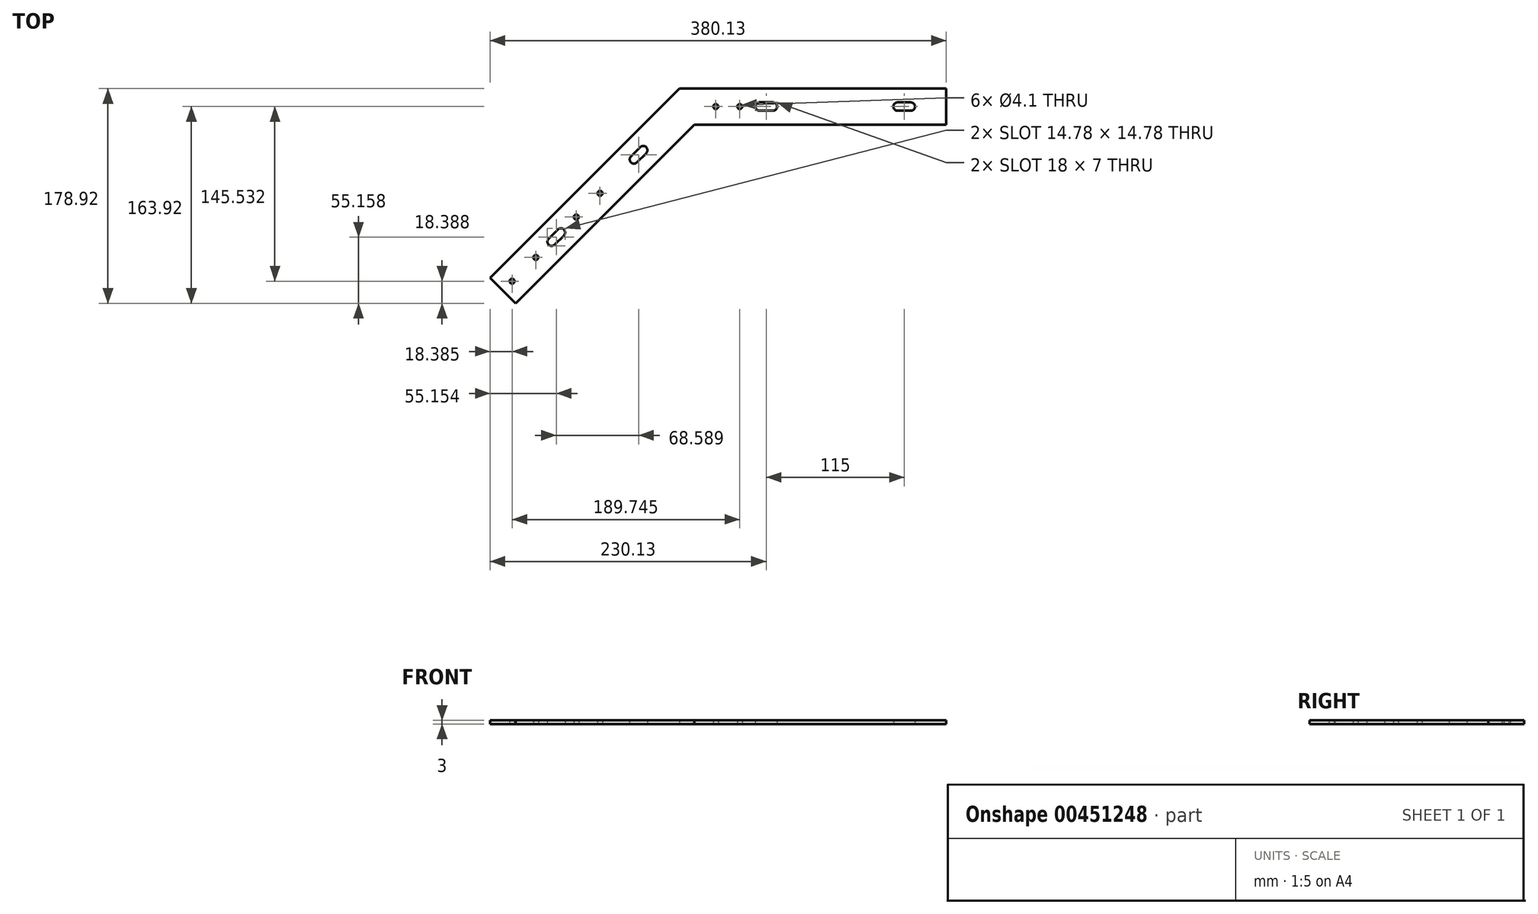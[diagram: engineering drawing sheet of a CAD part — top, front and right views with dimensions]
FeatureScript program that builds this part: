
annotation { "Feature Type Name" : "Feature", "Feature Type Description" : "" }
export const myFeature = defineFeature(function(context is Context, id is Id, definition is map)
    precondition{}
    {
        {
            var Q0;
            Q0=qCreatedBy(makeId("Top.planeOp"),FACE);
            var sketch = newSketch(context, id + "F0", { "sketchPlane" : qUnion([Q0])});
            skLineSegment(sketch, "E0", {"start": v(0, 0) * mm, "end": v(0, 30) * mm});
            skLineSegment(sketch, "E1", {"start": v(0, 30) * mm, "end": v(-222.43, 30) * mm});
            skLineSegment(sketch, "E2", {"start": v(-222.43, 30) * mm, "end": v(-380.13, -127.7) * mm});
            skLineSegment(sketch, "E3", {"start": v(-380.13, -127.7) * mm, "end": v(-358.92, -148.92) * mm});
            skLineSegment(sketch, "E4", {"start": v(-358.92, -148.92) * mm, "end": v(-210, 0) * mm});
            skLineSegment(sketch, "E5", {"start": v(0, 0) * mm, "end": v(-210, 0) * mm});
            skLineSegment(sketch, "E6", {"start": v(-222.43, 30) * mm, "end": v(-210, 0) * mm, "construction": true});
            skPoint(sketch, "E7.centerSnap0", {"position": v(0, 15) * mm});
            skCircle(sketch, "E8", {"center": v(-324.98, -93.76) * mm, "radius": 3.5 * mm, "construction": true});
            skLineSegment(sketch, "E9.bottom", {"start": v(-29.5, 11.5) * mm, "end": v(-40.5, 11.5) * mm});
            skLineSegment(sketch, "E9.top", {"start": v(-29.5, 18.5) * mm, "end": v(-40.5, 18.5) * mm});
            skLineSegment(sketch, "E9.left", {"start": v(-29.5, 11.5) * mm, "end": v(-29.5, 18.5) * mm});
            skLineSegment(sketch, "E9.right", {"start": v(-40.5, 11.5) * mm, "end": v(-40.5, 18.5) * mm});
            skPoint(sketch, "E9.middle", {"position": v(-35, 15) * mm});
            skArc(sketch, "E10", {"start": v(-40.5, 18.5) * mm, "mid": v(-44, 15) * mm, "end": v(-40.5, 11.5) * mm});
            skArc(sketch, "E11", {"start": v(-29.5, 11.5) * mm, "mid": v(-26, 15) * mm, "end": v(-29.5, 18.5) * mm});
            skLineSegment(sketch, "E12.bottom", {"start": v(-144.5, 11.5) * mm, "end": v(-155.5, 11.5) * mm});
            skLineSegment(sketch, "E12.top", {"start": v(-144.5, 18.5) * mm, "end": v(-155.5, 18.5) * mm});
            skLineSegment(sketch, "E12.left", {"start": v(-144.5, 11.5) * mm, "end": v(-144.5, 18.5) * mm});
            skLineSegment(sketch, "E12.right", {"start": v(-155.5, 11.5) * mm, "end": v(-155.5, 18.5) * mm});
            skPoint(sketch, "E12.middle", {"position": v(-150, 15) * mm});
            skArc(sketch, "E13", {"start": v(-155.5, 18.5) * mm, "mid": v(-159, 15) * mm, "end": v(-155.5, 11.5) * mm});
            skArc(sketch, "E14", {"start": v(-144.5, 11.5) * mm, "mid": v(-141, 15) * mm, "end": v(-144.5, 18.5) * mm});
            skLineSegment(sketch, "E15.bottom", {"start": v(-318.61, -92.35) * mm, "end": v(-326.39, -100.13) * mm});
            skLineSegment(sketch, "E15.top", {"start": v(-323.56, -87.4) * mm, "end": v(-331.34, -95.18) * mm});
            skLineSegment(sketch, "E15.left", {"start": v(-318.61, -92.35) * mm, "end": v(-323.56, -87.4) * mm});
            skLineSegment(sketch, "E15.right", {"start": v(-326.39, -100.13) * mm, "end": v(-331.34, -95.18) * mm});
            skArc(sketch, "E16", {"start": v(-331.34, -95.18) * mm, "mid": v(-331.34, -100.13) * mm, "end": v(-326.39, -100.13) * mm});
            skArc(sketch, "E17", {"start": v(-318.61, -92.35) * mm, "mid": v(-318.61, -87.4) * mm, "end": v(-323.56, -87.4) * mm});
            skCircle(sketch, "E18", {"center": v(-172, 15) * mm, "radius": 2.05 * mm});
            skCircle(sketch, "E19", {"center": v(-341.95, -110.73) * mm, "radius": 2.05 * mm});
            skCircle(sketch, "E20", {"center": v(-192, 15) * mm, "radius": 2.05 * mm});
            skLineSegment(sketch, "E21", {"start": v(-210, 0) * mm, "end": v(-164.47, 45.53) * mm, "construction": true});
            skLineSegment(sketch, "E22", {"start": v(-222.43, 30) * mm, "end": v(-201.21, 51.21) * mm, "construction": true});
            skLineSegment(sketch, "E23", {"start": v(-180, 30) * mm, "end": v(-201.21, 51.21) * mm, "construction": true});
            skLineSegment(sketch, "E24", {"start": v(-210, 0) * mm, "end": v(-290.3, 0) * mm, "construction": true});
            skCircle(sketch, "E25", {"center": v(-361.75, -130.53) * mm, "radius": 2.05 * mm});
            skCircle(sketch, "E26", {"center": v(-288.49, -57.28) * mm, "radius": 2.05 * mm});
            skCircle(sketch, "E27", {"center": v(-308.29, -77.07) * mm, "radius": 2.05 * mm});
            skCircle(sketch, "E28", {"center": v(-256.39, -25.17) * mm, "radius": 3.5 * mm, "construction": true});
            skLineSegment(sketch, "E29.bottom", {"start": v(-250.02, -23.76) * mm, "end": v(-257.8, -31.54) * mm});
            skLineSegment(sketch, "E29.top", {"start": v(-254.97, -18.8) * mm, "end": v(-262.75, -26.59) * mm});
            skLineSegment(sketch, "E29.left", {"start": v(-250.02, -23.76) * mm, "end": v(-254.97, -18.8) * mm});
            skLineSegment(sketch, "E29.right", {"start": v(-257.8, -31.54) * mm, "end": v(-262.75, -26.59) * mm});
            skArc(sketch, "E30", {"start": v(-262.75, -26.59) * mm, "mid": v(-262.75, -31.54) * mm, "end": v(-257.8, -31.54) * mm});
            skArc(sketch, "E31", {"start": v(-250.02, -23.76) * mm, "mid": v(-250.02, -18.8) * mm, "end": v(-254.97, -18.8) * mm});
            skLineSegment(sketch, "E32", {"start": v(-210, -9.14) * mm, "end": v(-150, -9.14) * mm, "construction": true});
            skSolve(sketch);
        }
        {
            var Q0;
            Q0 = qSketchRegion(id + "F0", true);
            extrude(context, id + "F1", {"entities" : qUnion([Q0]), "depth" : 3 * mm, "offsetDistance" : 25 * mm});
        }
    });
